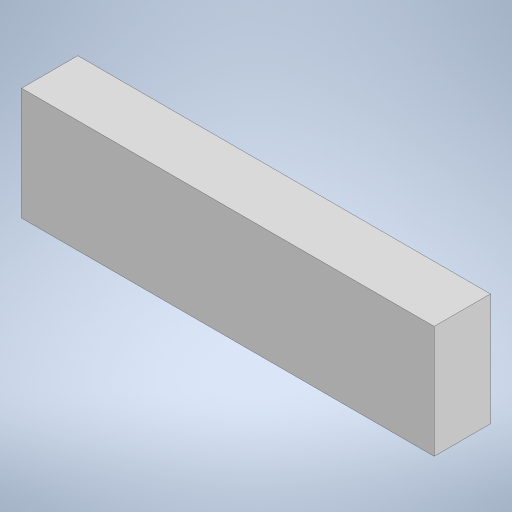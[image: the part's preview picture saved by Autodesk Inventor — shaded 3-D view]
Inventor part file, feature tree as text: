
AUTODESK INVENTOR PART (.ipt)
format: ipt  version: 2023 (Build 270158000, 158)  size: 205,824 bytes
history: native  units: mm
features: extrude x1, sketch x1
ambient origin geometry x8: Origin, YZ Plane, XZ Plane, XY Plane, X Axis, Y Axis, Z Axis, Center Point
bodies: Solid1 (feature_tree)
feature tree (2):
  extrude  "Extrusion1"  Depth=15.0mm
  sketch  "Sketch1"  dims[d0=30.0mm d1=15.0mm d2=110.0mm d3=0.0mm]
